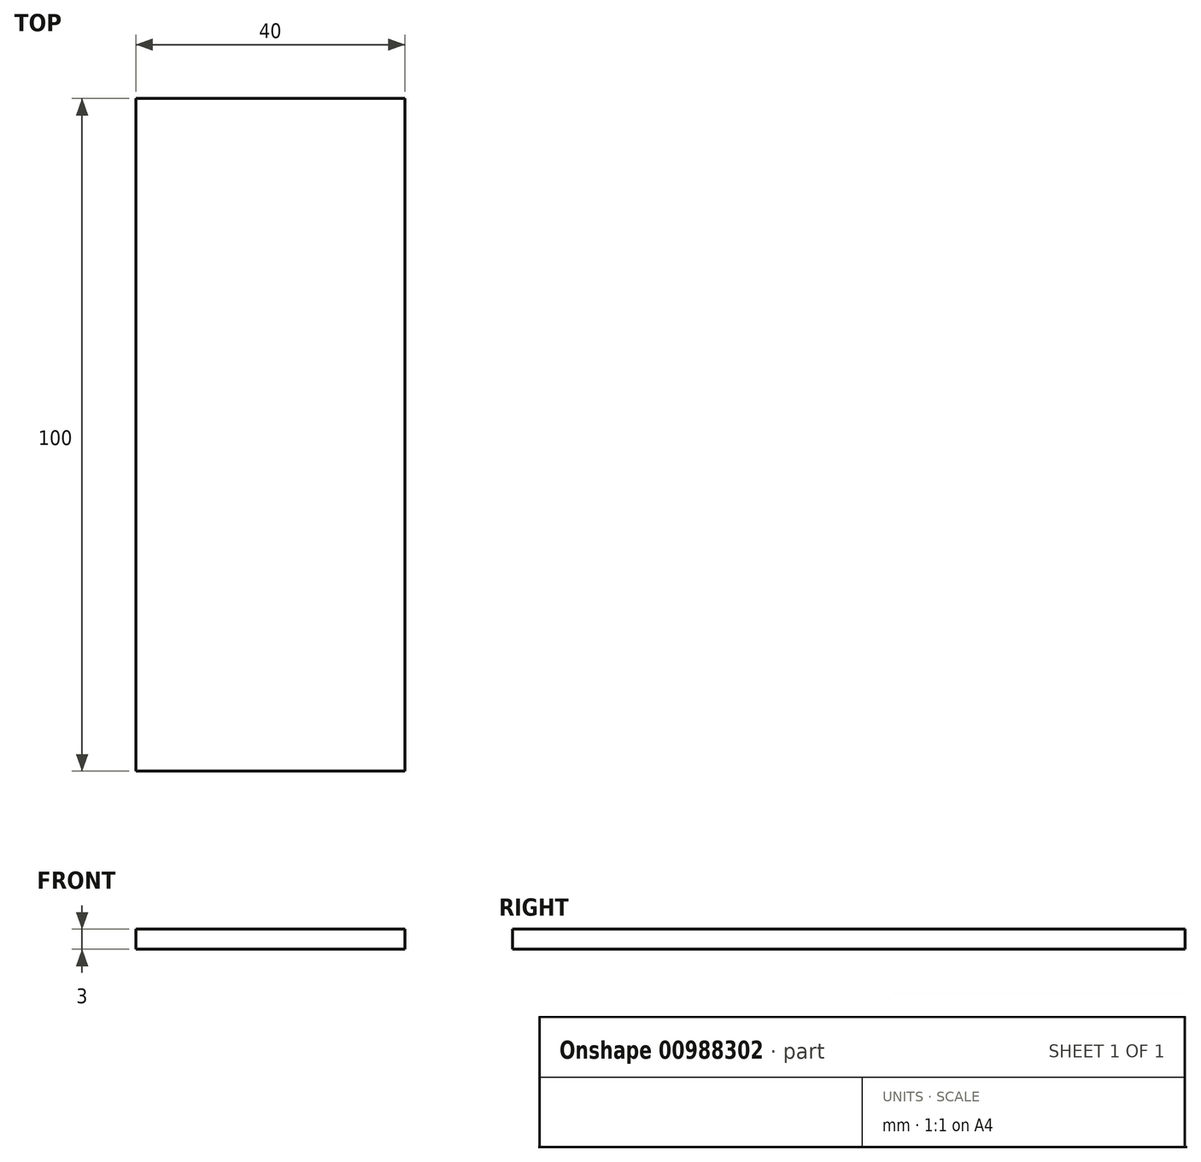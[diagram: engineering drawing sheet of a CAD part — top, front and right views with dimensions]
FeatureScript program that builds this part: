
annotation { "Feature Type Name" : "Feature", "Feature Type Description" : "" }
export const myFeature = defineFeature(function(context is Context, id is Id, definition is map)
    precondition{}
    {
        {
            var Q0;
            Q0=qCreatedBy(makeId("Top.planeOp"),FACE);
            var sketch = newSketch(context, id + "F0", { "sketchPlane" : qUnion([Q0])});
            skLineSegment(sketch, "E0.bottom", {"start": v(0, 100) * mm, "end": v(40, 100) * mm});
            skLineSegment(sketch, "E0.top", {"start": v(0, 0) * mm, "end": v(40, 0) * mm});
            skLineSegment(sketch, "E0.left", {"start": v(0, 100) * mm, "end": v(0, 0) * mm});
            skLineSegment(sketch, "E0.right", {"start": v(40, 100) * mm, "end": v(40, 0) * mm});
            skSolve(sketch);
        }
        {
            var Q0;
            Q0=makeQuery(id+"F0.imprint","IMPRINT",FACE,{"disambiguationData":[TD([[makeQuery(id+"F0.imprint","IMPRINT",EDGE,{"derivedFrom":sQuery(id+"F0.wireOp",EDGE,"E0.bottom")}),-1.0]])]});
            extrude(context, id + "F1", {"entities" : qUnion([Q0]), "depth" : 3 * mm, "offsetDistance" : 25 * mm});
        }
    });
